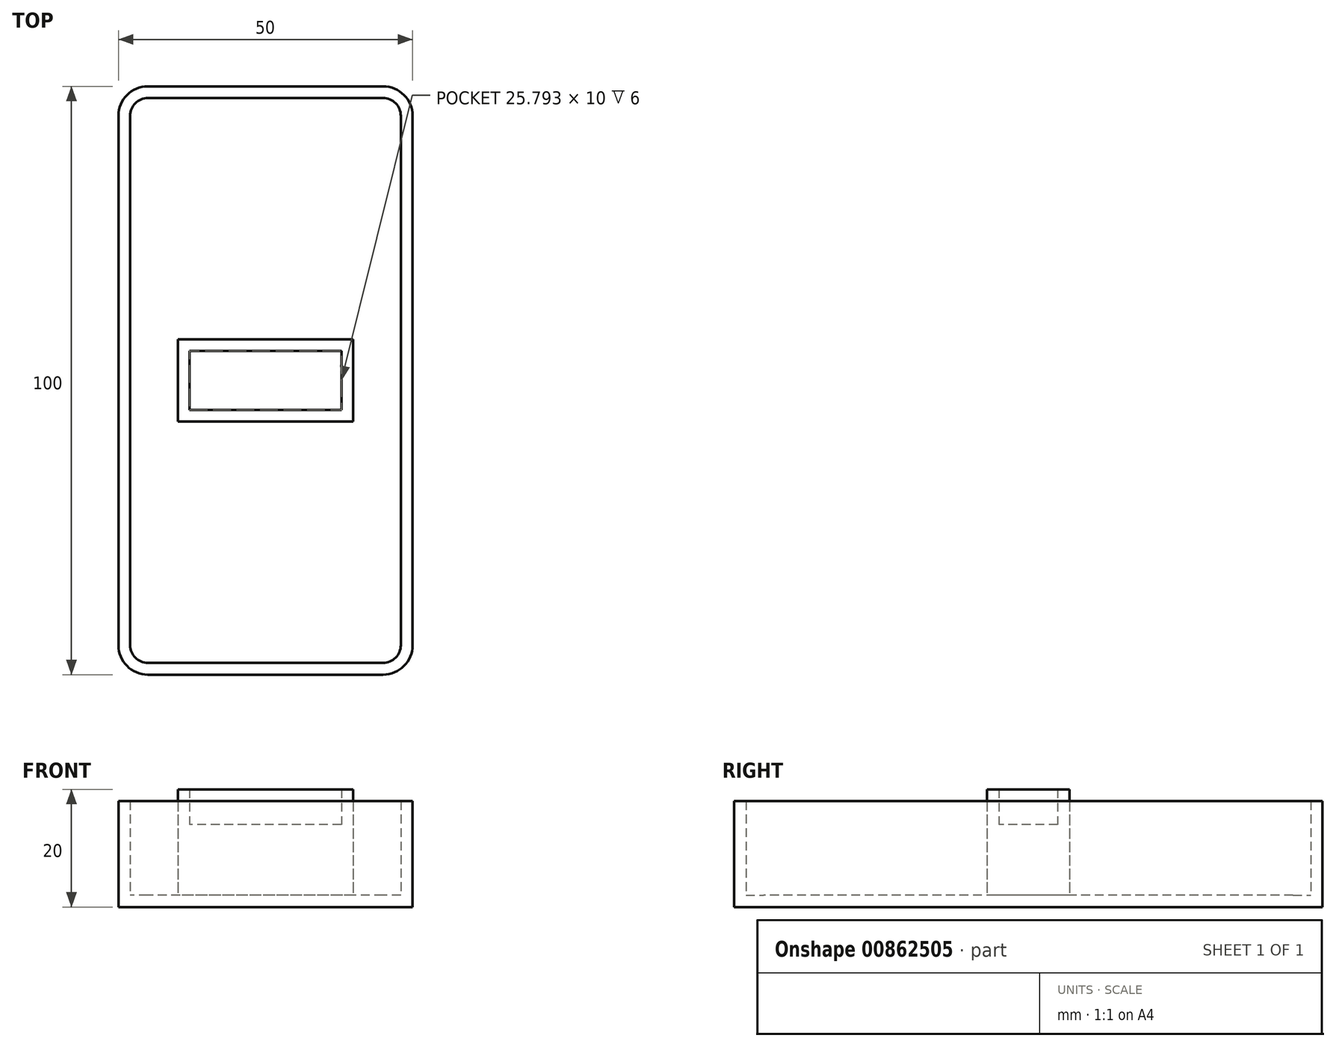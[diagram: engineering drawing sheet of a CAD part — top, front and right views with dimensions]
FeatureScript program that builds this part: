
annotation { "Feature Type Name" : "Feature", "Feature Type Description" : "" }
export const myFeature = defineFeature(function(context is Context, id is Id, definition is map)
    precondition{}
    {
        {
            var Q0;
            Q0=qCreatedBy(makeId("Top.planeOp"),FACE);
            var sketch = newSketch(context, id + "F0", { "sketchPlane" : qUnion([Q0])});
            skLineSegment(sketch, "E0.bottom", {"start": v(12.9, 5) * mm, "end": v(-12.9, 5) * mm});
            skLineSegment(sketch, "E0.top", {"start": v(12.9, -5) * mm, "end": v(-12.9, -5) * mm});
            skLineSegment(sketch, "E0.left", {"start": v(12.9, 5) * mm, "end": v(12.9, -5) * mm});
            skLineSegment(sketch, "E0.right", {"start": v(-12.9, 5) * mm, "end": v(-12.9, -5) * mm});
            skPoint(sketch, "E0.middle", {"position": v(0, 0) * mm});
            skLineSegment(sketch, "E1.bottom", {"start": v(25, 50) * mm, "end": v(-25, 50) * mm});
            skLineSegment(sketch, "E1.top", {"start": v(25, -50) * mm, "end": v(-25, -50) * mm});
            skLineSegment(sketch, "E1.left", {"start": v(25, 50) * mm, "end": v(25, -50) * mm});
            skLineSegment(sketch, "E1.right", {"start": v(-25, 50) * mm, "end": v(-25, -50) * mm});
            skSolve(sketch);
        }
        {
            var Q0;
            Q0=makeQuery(id+"F0.imprint","IMPRINT",FACE,{"disambiguationData":[TD([[makeQuery(id+"F0.imprint","IMPRINT",EDGE,{"derivedFrom":sQuery(id+"F0.wireOp",EDGE,"E0.bottom")}),-1.0]])]});
            extrude(context, id + "F1", {"entities" : qUnion([Q0]), "depth" : 20 * mm, "offsetDistance" : 25 * mm});
        }
        {
            var Q0;
            Q0=makeQuery(id+"F1.opExtrude","SWEPT_EDGE",EDGE,{"disambiguationData":[OSD([sQuery(id+"F0.wireOp",EDGE,"E1.top"),sQuery(id+"F0.wireOp",EDGE,"E1.right")])]});
            var Q1;
            Q1=makeQuery(id+"F1.opExtrude","SWEPT_EDGE",EDGE,{"disambiguationData":[OSD([sQuery(id+"F0.wireOp",EDGE,"E1.top"),sQuery(id+"F0.wireOp",EDGE,"E1.left")])]});
            var Q2;
            Q2=makeQuery(id+"F1.opExtrude","SWEPT_EDGE",EDGE,{"disambiguationData":[OSD([sQuery(id+"F0.wireOp",EDGE,"E1.bottom"),sQuery(id+"F0.wireOp",EDGE,"E1.right")])]});
            var Q3;
            Q3=makeQuery(id+"F1.opExtrude","SWEPT_EDGE",EDGE,{"disambiguationData":[OSD([sQuery(id+"F0.wireOp",EDGE,"E1.bottom"),sQuery(id+"F0.wireOp",EDGE,"E1.left")])]});
            fillet(context, id + "F2", {"entities" : qUnion([Q0, Q1, Q2, Q3]), "radius" : 5 * mm, "tangentPropagation" : true, "allowEdgeOverflow" : false});
        }
        {
            var Q0;
            Q0=makeQuery(id+"F1.opExtrude","CAP_FACE",FACE,{"disambiguationData":[OSD([sQuery(id+"F0.wireOp",EDGE,"E0.bottom"),sQuery(id+"F0.wireOp",EDGE,"E0.top"),sQuery(id+"F0.wireOp",EDGE,"E0.left"),sQuery(id+"F0.wireOp",EDGE,"E0.right"),sQuery(id+"F0.wireOp",EDGE,"E1.bottom"),sQuery(id+"F0.wireOp",EDGE,"E1.top"),sQuery(id+"F0.wireOp",EDGE,"E1.left"),sQuery(id+"F0.wireOp",EDGE,"E1.right")])],"isStart":false});
            shell(context, id + "F3", {"entities" : qUnion([Q0]), "thickness" : 2 * mm});
        }
        {
            var Q0;
            {var subQ0=sQuery(id+"F0.wireOp",EDGE,"E1.right");var subQ1=sQuery(id+"F0.wireOp",EDGE,"E1.left");var subQ2=sQuery(id+"F0.wireOp",EDGE,"E1.top");var subQ3=sQuery(id+"F0.wireOp",EDGE,"E1.bottom");var subQ4=sQuery(id+"F0.wireOp",EDGE,"E0.right");var subQ5=sQuery(id+"F0.wireOp",EDGE,"E0.left");var subQ6=sQuery(id+"F0.wireOp",EDGE,"E0.top");var subQ7=sQuery(id+"F0.wireOp",EDGE,"E0.bottom");Q0=makeQuery(id+"F3.opShell","OFFSET_FACE",FACE,{"disambiguationData":[OSD([subQ7,subQ6,subQ5,subQ4,subQ3,subQ2,subQ1,subQ0]),TDD([makeQuery(id+"F1.opExtrude","CAP_FACE",FACE,{"disambiguationData":[OSD([subQ7,subQ6,subQ5,subQ4,subQ3,subQ2,subQ1,subQ0])],"isStart":false})])]});}
            extrude(context, id + "F4", {"entities" : qUnion([Q0]), "operationType" : NewBodyOperationType.REMOVE, "oppositeDirection" : true, "depth" : 2 * mm, "offsetDistance" : 25 * mm});
        }
        {
            var Q0;
            Q0=makeQuery(id+"F0.imprint","IMPRINT",FACE,{"disambiguationData":[TD([[makeQuery(id+"F0.imprint","IMPRINT",EDGE,{"derivedFrom":sQuery(id+"F0.wireOp",EDGE,"E0.bottom")}),1.0]])]});
            extrude(context, id + "F5", {"entities" : qUnion([Q0]), "operationType" : NewBodyOperationType.ADD, "depth" : 14 * mm, "offsetDistance" : 25 * mm});
        }
    });
